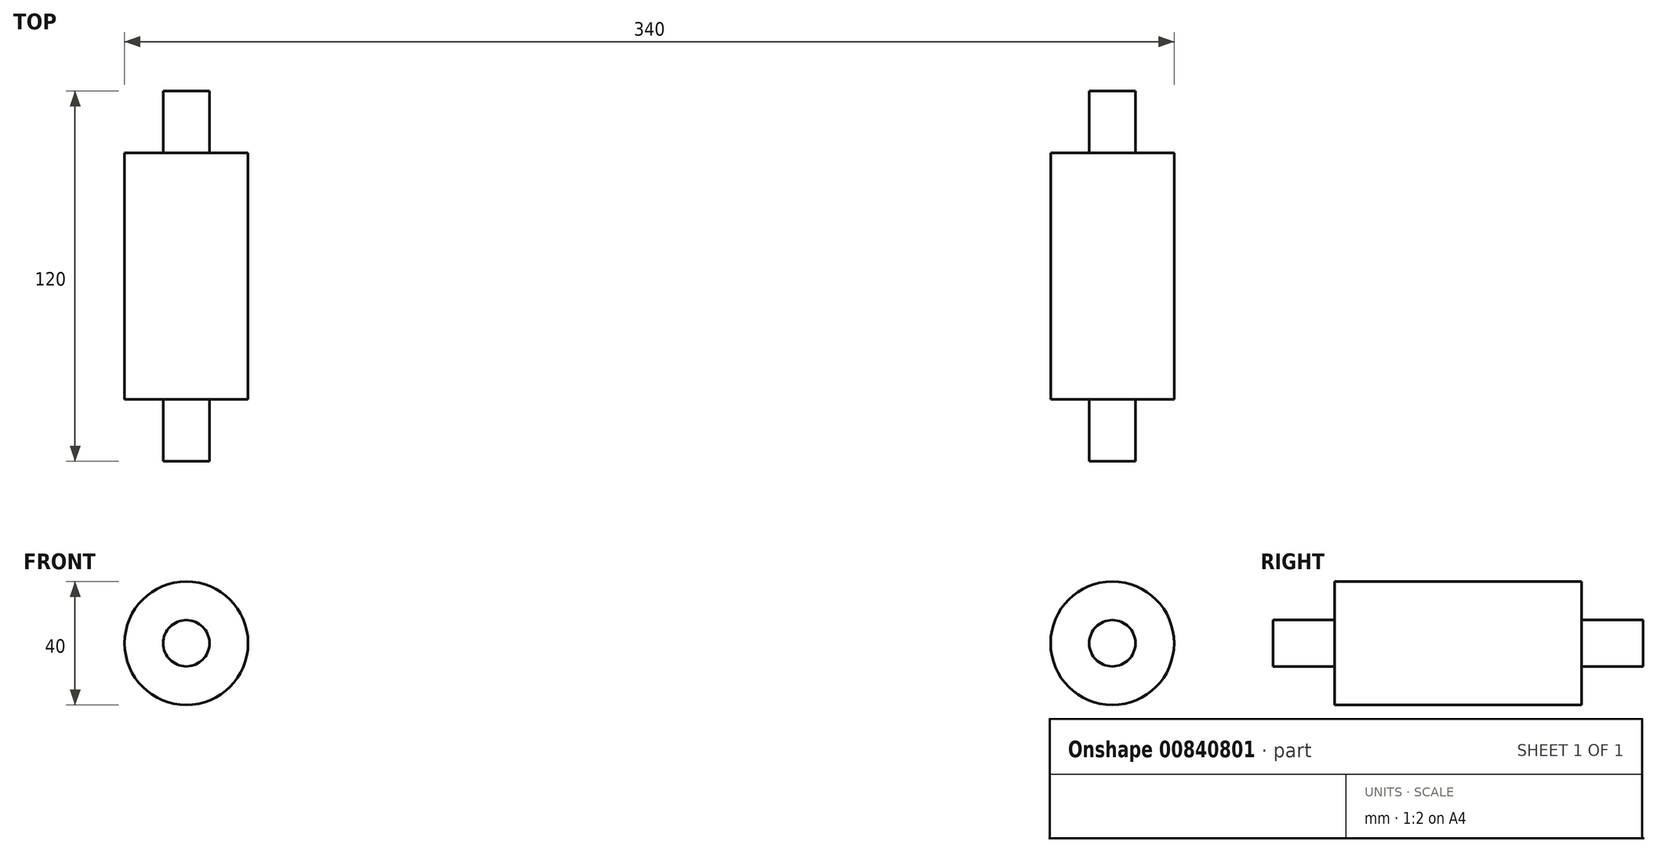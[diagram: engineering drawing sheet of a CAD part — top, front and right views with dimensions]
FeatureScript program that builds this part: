
annotation { "Feature Type Name" : "Feature", "Feature Type Description" : "" }
export const myFeature = defineFeature(function(context is Context, id is Id, definition is map)
    precondition{}
    {
        {
            var Q0;
            Q0=qCreatedBy(makeId("Front.planeOp"),FACE);
            var sketch = newSketch(context, id + "F0", { "sketchPlane" : qUnion([Q0])});
            skCircle(sketch, "E0", {"center": v(-150, 0) * mm, "radius": 20 * mm});
            skCircle(sketch, "E1", {"center": v(150, 0) * mm, "radius": 20 * mm});
            skSolve(sketch);
        }
        {
            var Q0;
            Q0=makeQuery(id+"F0.imprint","IMPRINT",FACE,{"disambiguationData":[TD([[makeQuery(id+"F0.imprint","IMPRINT",EDGE,{"derivedFrom":sQuery(id+"F0.wireOp",EDGE,"E0")}),1.0]])]});
            extrude(context, id + "F1", {"entities" : qUnion([Q0]), "depth" : 80 * mm, "offsetDistance" : 25 * mm});
        }
        {
            var Q0;
            Q0=makeQuery(id+"F0.imprint","IMPRINT",FACE,{"disambiguationData":[TD([[makeQuery(id+"F0.imprint","IMPRINT",EDGE,{"derivedFrom":sQuery(id+"F0.wireOp",EDGE,"E1")}),1.0]])]});
            extrude(context, id + "F2", {"entities" : qUnion([Q0]), "depth" : 80 * mm, "offsetDistance" : 25 * mm});
        }
        {
            var Q0;
            Q0=makeQuery(id+"F1.opExtrude","CAP_FACE",FACE,{"disambiguationData":[OSD([sQuery(id+"F0.wireOp",EDGE,"E0")])],"isStart":false});
            var sketch = newSketch(context, id + "F3", { "sketchPlane" : qUnion([Q0])});
            skCircle(sketch, "E2", {"center": v(-150, 0) * mm, "radius": 7.5 * mm});
            skSolve(sketch);
        }
        {
            var Q0;
            Q0 = qSketchRegion(id + "F3", true);
            extrude(context, id + "F4", {"entities" : qUnion([Q0]), "operationType" : NewBodyOperationType.ADD, "depth" : 20 * mm, "offsetDistance" : 25 * mm});
        }
        {
            var Q0;
            Q0=makeQuery(id+"F0.imprint","IMPRINT",FACE,{"disambiguationData":[TD([[makeQuery(id+"F0.imprint","IMPRINT",EDGE,{"derivedFrom":sQuery(id+"F0.wireOp",EDGE,"E0")}),1.0]])]});
            var sketch = newSketch(context, id + "F5", { "sketchPlane" : qUnion([Q0])});
            skCircle(sketch, "E3", {"center": v(-150, 0) * mm, "radius": 7.5 * mm});
            skSolve(sketch);
        }
        {
            var Q0;
            Q0 = qSketchRegion(id + "F5", true);
            extrude(context, id + "F6", {"entities" : qUnion([Q0]), "operationType" : NewBodyOperationType.ADD, "oppositeDirection" : true, "depth" : 20 * mm, "offsetDistance" : 25 * mm});
        }
        {
            var Q0;
            Q0=makeQuery(id+"F2.opExtrude","CAP_FACE",FACE,{"disambiguationData":[OSD([sQuery(id+"F0.wireOp",EDGE,"E1")])],"isStart":false});
            var sketch = newSketch(context, id + "F7", { "sketchPlane" : qUnion([Q0])});
            skCircle(sketch, "E4", {"center": v(150, 0) * mm, "radius": 7.5 * mm});
            skSolve(sketch);
        }
        {
            var Q0;
            Q0 = qSketchRegion(id + "F7", true);
            extrude(context, id + "F8", {"entities" : qUnion([Q0]), "operationType" : NewBodyOperationType.ADD, "depth" : 20 * mm, "offsetDistance" : 25 * mm});
        }
        {
            var Q0;
            Q0=makeQuery(id+"F0.imprint","IMPRINT",FACE,{"disambiguationData":[TD([[makeQuery(id+"F0.imprint","IMPRINT",EDGE,{"derivedFrom":sQuery(id+"F0.wireOp",EDGE,"E1")}),1.0]])]});
            var sketch = newSketch(context, id + "F9", { "sketchPlane" : qUnion([Q0])});
            skCircle(sketch, "E5", {"center": v(150, 0) * mm, "radius": 7.5 * mm});
            skSolve(sketch);
        }
        {
            var Q0;
            Q0 = qSketchRegion(id + "F9", true);
            extrude(context, id + "F10", {"entities" : qUnion([Q0]), "operationType" : NewBodyOperationType.ADD, "oppositeDirection" : true, "depth" : 20 * mm, "offsetDistance" : 25 * mm});
        }
    });
